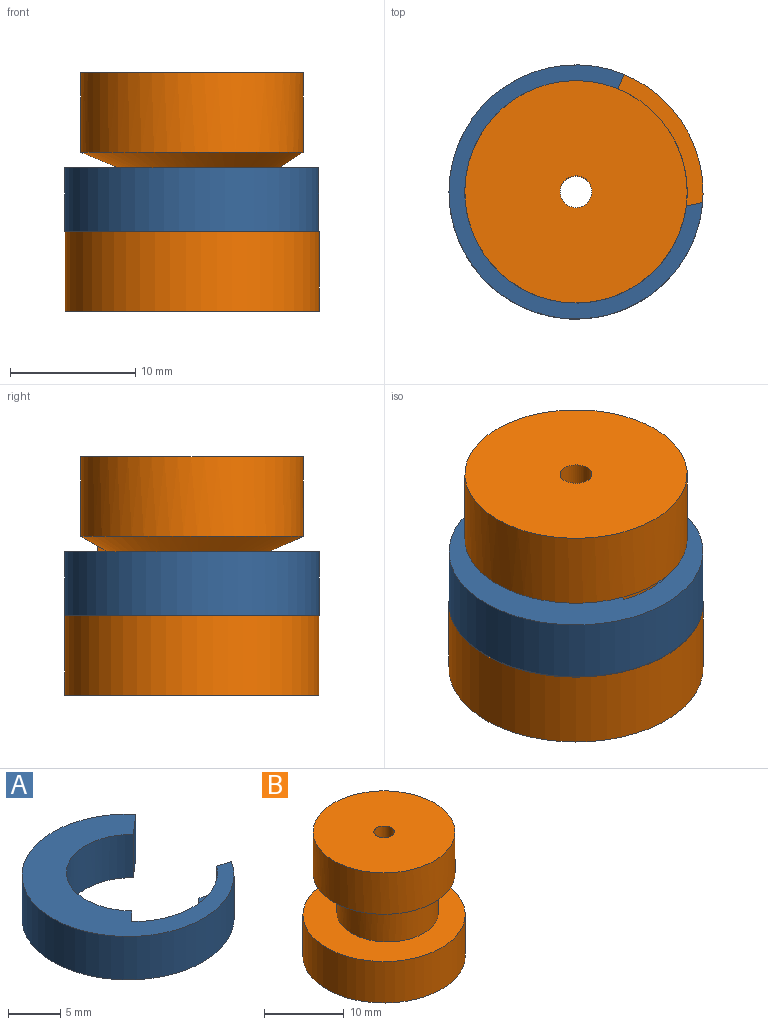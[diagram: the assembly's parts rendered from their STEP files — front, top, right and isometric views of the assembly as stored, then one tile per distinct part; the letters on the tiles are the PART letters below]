
ASSEMBLY  parts=2 mates=1
PART A: 9 faces, bbox 18.8x20.3x5.1 mm
  f0: cylinder r=10.16mm len=20.32mm, axis (0,0,-1), area 258.9mm2, adj f1,f2,f4,f5
  f1: plane 20.32x18.78mm, normal (0,0,1), area 139.7mm2, adj f0,f3,f4,f5,f6,f7
  f2: plane 20.32x18.78mm, normal (0,0,-1), area 161mm2, adj f0,f3,f4,f5
  f3: cylinder r=6.35mm len=12.7mm, axis (0,0,1), area 121.9mm2, adj f1,f2,f4,f5,f6,f8
  f4: plane 5.08x2.53mm, normal (0.65,-0.76,0), area 17mm2, adj f0,f1,f2,f3
  f5: plane 5.08x3.45mm, normal (0.26,0.97,0), area 12.2mm2, adj f0,f1,f2,f3,f7,f8
  f6: plane 3.05x1.27mm, normal (0.7,-0.71,0), area 5.4mm2, adj f1,f3,f7,f8
  f7: cylinder r=8.13mm len=12.25mm, axis (0,0,1), area 42.4mm2, adj f1,f5,f6,f8
  f8: plane 12.25x3.68mm, normal (0,0,1), area 21.3mm2, adj f3,f5,f6,f7
PART B: 12 faces, bbox 20.3x20.3x19.1 mm
  f0: plane 3.34x0.93mm, normal (-0.7,0.71,0), area 2.9mm2, adj f2,f3,f10,f11
  f1: plane 3.37x1.13mm, normal (0.49,-0.87,0), area 2.9mm2, adj f2,f3,f10,f11
  f2: cylinder r=6.35mm len=12.7mm, axis (0,0,-1), area 198.5mm2, adj f0,f1,f3,f5,f11
  f3: bspline ~17.77x17.76mm, area 133.6mm2, adj f0,f1,f2,f8,f10
  f4: cylinder r=10.16mm len=20.32mm, axis (0,0,-1), area 405.4mm2, adj f5,f6
  f5: plane 20.32x20.32mm, normal (0,0,1), area 197.6mm2, adj f2,f4
  f6: plane 20.32x20.32mm, normal (0,0,-1), area 319.2mm2, adj f4,f9
  f7: plane 17.78x17.78mm, normal (0,0,1), area 243.2mm2, adj f8,f9
  f8: cylinder r=8.89mm len=17.78mm, axis (0,0,-1), area 354.7mm2, adj f3,f7
  f9: cylinder r=1.27mm len=19.05mm, axis (0,0,1), area 152mm2, adj f6,f7
  f10: cylinder r=7.62mm len=2.08mm, axis (0,0,1), area 4.1mm2, adj f0,f1,f3,f11
  f11: cone r=6.35mm half-angle=45deg, axis (0,0,1), area 3.3mm2, adj f0,f1,f2,f10
PLACE A rot(axis=(0,0,1),27.2deg) t=(11.3,11.89,4.22)mm
PLACE B rot(axis=(0,0,1),27.2deg) t=(11.3,11.89,-2.16)mm
MATE slider B.f2 <-> A.f7  axis (0,0,-1) through (11.87,12.18,6.74)mm
